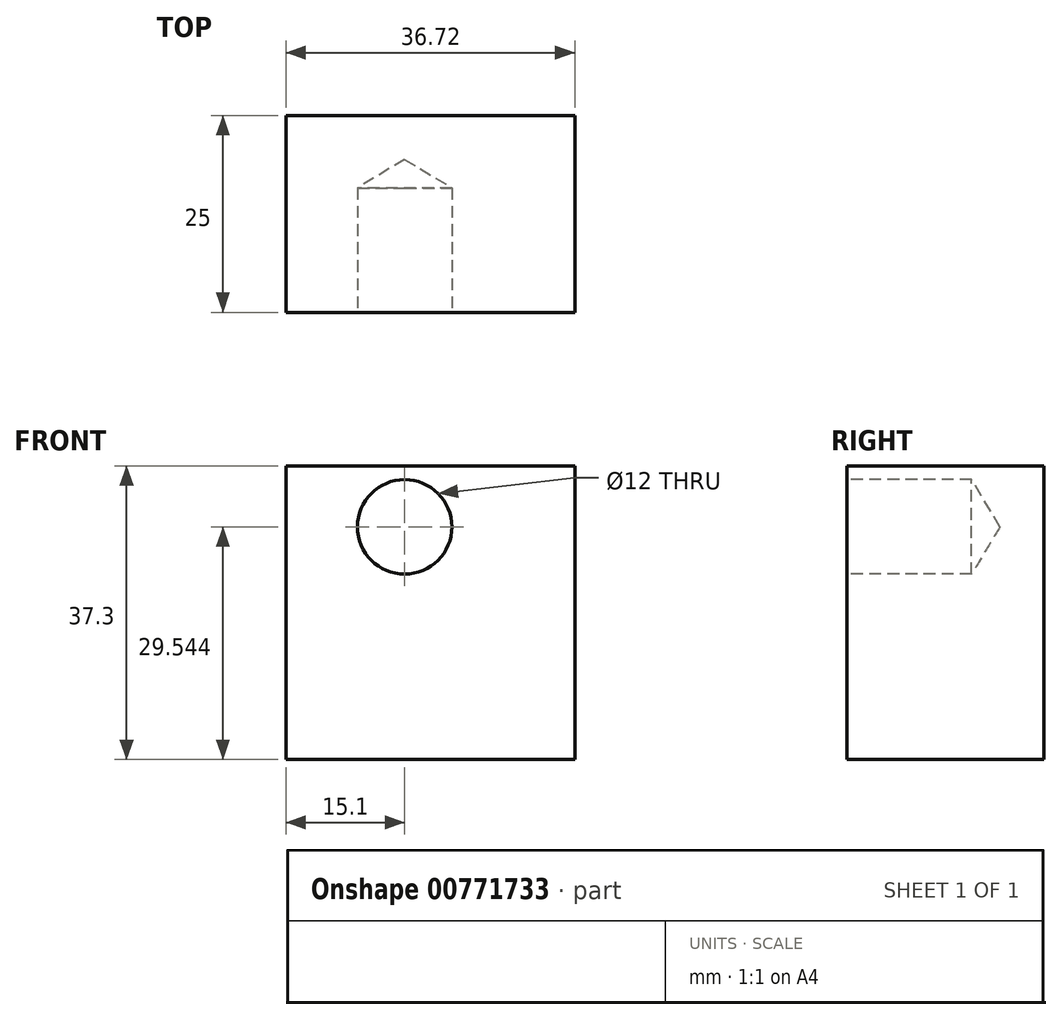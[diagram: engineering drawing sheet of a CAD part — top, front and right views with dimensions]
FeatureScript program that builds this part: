
annotation { "Feature Type Name" : "Feature", "Feature Type Description" : "" }
export const myFeature = defineFeature(function(context is Context, id is Id, definition is map)
    precondition{}
    {
        {
            var Q0;
            Q0=qCreatedBy(makeId("Front.planeOp"),FACE);
            var sketch = newSketch(context, id + "F0", { "sketchPlane" : qUnion([Q0])});
            skLineSegment(sketch, "E0.bottom", {"start": v(-118.66, 8.97) * mm, "end": v(-81.94, 8.97) * mm});
            skLineSegment(sketch, "E0.top", {"start": v(-118.66, 46.27) * mm, "end": v(-81.94, 46.27) * mm});
            skLineSegment(sketch, "E0.left", {"start": v(-118.66, 8.97) * mm, "end": v(-118.66, 46.27) * mm});
            skLineSegment(sketch, "E0.right", {"start": v(-81.94, 8.97) * mm, "end": v(-81.94, 46.27) * mm});
            skPoint(sketch, "E0.middle", {"position": v(-100.3, 27.62) * mm});
            skSolve(sketch);
        }
        {
            var Q0;
            Q0=makeQuery(id+"F0.imprint","IMPRINT",FACE,{"disambiguationData":[TD([[makeQuery(id+"F0.imprint","IMPRINT",EDGE,{"derivedFrom":sQuery(id+"F0.wireOp",EDGE,"E0.bottom")}),1.0]])]});
            extrude(context, id + "F1", {"entities" : qUnion([Q0]), "depth" : 25 * mm, "offsetDistance" : 25 * mm});
        }
        {
            var Q0;
            Q0=makeQuery(id+"F1.opExtrude","CAP_FACE",FACE,{"disambiguationData":[OSD([sQuery(id+"F0.wireOp",EDGE,"E0.bottom"),sQuery(id+"F0.wireOp",EDGE,"E0.top"),sQuery(id+"F0.wireOp",EDGE,"E0.left"),sQuery(id+"F0.wireOp",EDGE,"E0.right")])],"isStart":false});
            var sketch = newSketch(context, id + "F2", { "sketchPlane" : qUnion([Q0])});
            skPoint(sketch, "E1", {"position": v(-103.56, 38.51) * mm});
            skSolve(sketch);
        }
        {
            var Q0;
            Q0=sQuery(id+"F2.wireOp",VERTEX,"E1");
            var Q1;
            Q1=makeQuery(id+"F1.opExtrude","SWEPT_BODY",BODY,{"disambiguationData":[OSD([sQuery(id+"F0.wireOp",EDGE,"E0.bottom"),sQuery(id+"F0.wireOp",EDGE,"E0.top"),sQuery(id+"F0.wireOp",EDGE,"E0.left"),sQuery(id+"F0.wireOp",EDGE,"E0.right")])]});
            hole(context, id + "F3", {"style" : HoleStyle.SIMPLE, "endStyle" : HoleEndStyle.BLIND, "holeDiameter" : 12 * mm, "majorDiameter" : 5 * mm, "holeDepth" : 15.8 * mm, "isTappedThrough" : true, "tappedDepth" : 12 * mm, "tapClearance" : 3, "locations" : qUnion([Q0]), "scope" : qUnion([Q1])});
        }
    });
